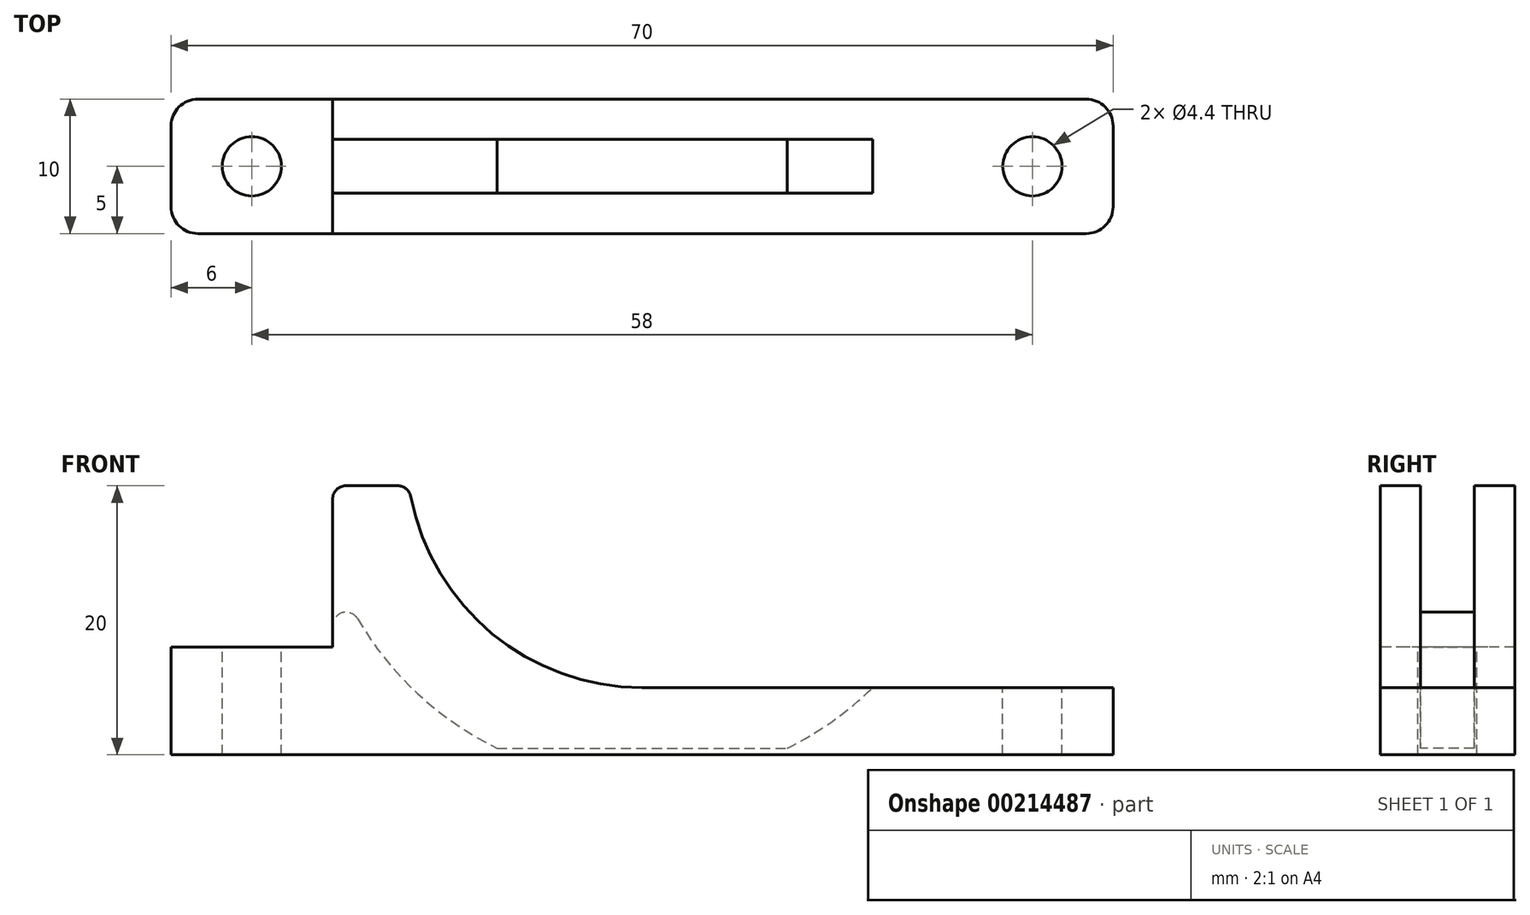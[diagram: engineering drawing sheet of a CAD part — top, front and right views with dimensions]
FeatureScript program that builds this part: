
annotation { "Feature Type Name" : "Feature", "Feature Type Description" : "" }
export const myFeature = defineFeature(function(context is Context, id is Id, definition is map)
    precondition{}
    {
        {
            var Q0;
            Q0=qCreatedBy(makeId("Top.planeOp"),FACE);
            var sketch = newSketch(context, id + "F0", { "sketchPlane" : qUnion([Q0])});
            skLineSegment(sketch, "E0.bottom", {"start": v(35, 5) * mm, "end": v(-35, 5) * mm});
            skLineSegment(sketch, "E0.top", {"start": v(35, -5) * mm, "end": v(-35, -5) * mm});
            skLineSegment(sketch, "E0.left", {"start": v(35, 5) * mm, "end": v(35, -5) * mm});
            skLineSegment(sketch, "E0.right", {"start": v(-35, 5) * mm, "end": v(-35, -5) * mm});
            skPoint(sketch, "E0.middle", {"position": v(0, 0) * mm});
            skSolve(sketch);
        }
        {
            var Q0;
            Q0=makeQuery(id+"F0.imprint","IMPRINT",FACE,{"disambiguationData":[TD([[makeQuery(id+"F0.imprint","IMPRINT",EDGE,{"derivedFrom":sQuery(id+"F0.wireOp",EDGE,"E0.bottom")}),1.0]])]});
            extrude(context, id + "F1", {"entities" : qUnion([Q0]), "depth" : 8 * mm});
        }
        {
            var Q0;
            Q0=makeQuery(id+"F1.opExtrude","CAP_FACE",FACE,{"disambiguationData":[OSD([sQuery(id+"F0.wireOp",EDGE,"E0.bottom"),sQuery(id+"F0.wireOp",EDGE,"E0.top"),sQuery(id+"F0.wireOp",EDGE,"E0.left"),sQuery(id+"F0.wireOp",EDGE,"E0.right")])],"isStart":false});
            var sketch = newSketch(context, id + "F2", { "sketchPlane" : qUnion([Q0])});
            skLineSegment(sketch, "E1.bottom", {"start": v(-23, 5) * mm, "end": v(35, 5) * mm});
            skLineSegment(sketch, "E1.top", {"start": v(-23, -5) * mm, "end": v(35, -5) * mm});
            skLineSegment(sketch, "E1.left", {"start": v(-23, 5) * mm, "end": v(-23, -5) * mm});
            skLineSegment(sketch, "E1.right", {"start": v(35, 5) * mm, "end": v(35, -5) * mm});
            skSolve(sketch);
        }
        {
            var Q0;
            Q0=makeQuery(id+"F2.imprint","IMPRINT",FACE,{"disambiguationData":[TD([[makeQuery(id+"F2.imprint","IMPRINT",EDGE,{"derivedFrom":sQuery(id+"F2.wireOp",EDGE,"E1.bottom")}),1.0]])]});
            extrude(context, id + "F3", {"entities" : qUnion([Q0]), "operationType" : NewBodyOperationType.ADD, "depth" : 12 * mm});
        }
        {
            var Q0;
            Q0=qCreatedBy(makeId("Front.planeOp"),FACE);
            var sketch = newSketch(context, id + "F4", { "sketchPlane" : qUnion([Q0])});
            skCircle(sketch, "E2", {"center": v(0, 22.5) * mm, "radius": 17.5 * mm});
            skCircle(sketch, "E3", {"center": v(0, 22.5) * mm, "radius": 24.5 * mm});
            skLineSegment(sketch, "E4", {"start": v(-10.78, 0.5) * mm, "end": v(10.78, 0.5) * mm});
            skLineSegment(sketch, "E5", {"start": v(36.3, 25) * mm, "end": v(17.32, 25) * mm});
            skLineSegment(sketch, "E6", {"start": v(36.3, 25) * mm, "end": v(36.3, 5) * mm});
            skLineSegment(sketch, "E7", {"start": v(36.3, 5) * mm, "end": v(0, 5) * mm});
            skSolve(sketch);
        }
        {
            var Q0;
            Q0=makeQuery(id+"F4.imprint","IMPRINT",FACE,{"disambiguationData":[TD([[makeQuery(id+"F4.imprint","IMPRINT",EDGE,{"derivedFrom":sQuery(id+"F4.wireOp",EDGE,"E2")}),1.0]])]});
            var Q1;
            {var subQ0=sQuery(id+"F4.wireOp",EDGE,"E5");var subQ1=sQuery(id+"F4.wireOp",EDGE,"E2");var subQ2=makeQuery(id+"F4.imprint","INTERSECT",VERTEX,{"derivedFrom":[subQ1,subQ0]});Q1=makeQuery(id+"F4.imprint","IMPRINT",FACE,{"disambiguationData":[TD([[makeQuery(id+"F4.imprint","IMPRINT",EDGE,{"disambiguationData":[TD([[subQ2,1.0]])],"derivedFrom":subQ1}),-1.0]])]});}
            var Q2;
            {var subQ5=sQuery(id+"F4.wireOp",EDGE,"E6");Q2=makeQuery(id+"F4.imprint","IMPRINT",FACE,{"disambiguationData":[TD([[makeQuery(id+"F4.imprint","IMPRINT",EDGE,{"derivedFrom":subQ5}),-1.0]])]});}
            extrude(context, id + "F5", {"entities" : qUnion([Q0, Q1, Q2]), "operationType" : NewBodyOperationType.REMOVE, "endBound" : BoundingType.SYMMETRIC, "oppositeDirection" : true, "depth" : 15 * mm});
        }
        {
            var Q0;
            {var subQ0=sQuery(id+"F0.wireOp",EDGE,"E0.bottom");var subQ1=sQuery(id+"F0.wireOp",EDGE,"E0.top");var subQ2=sQuery(id+"F0.wireOp",EDGE,"E0.right");Q0=makeQuery(id+"F5.boolean.opBoolean","SPLIT",FACE,{"disambiguationData":[TD([makeQuery(id+"F1.opExtrude","SWEPT_FACE",FACE,{"disambiguationData":[OSD([subQ2])]})])],"derivedFrom":makeQuery(id+"F1.opExtrude","CAP_FACE",FACE,{"disambiguationData":[OSD([subQ0,subQ1,sQuery(id+"F0.wireOp",EDGE,"E0.left"),subQ2])],"isStart":false})});}
            var sketch = newSketch(context, id + "F6", { "sketchPlane" : qUnion([Q0])});
            skPoint(sketch, "E8", {"position": v(-29, 0) * mm});
            skPoint(sketch, "E9.MirrorP", {"position": v(29, 0) * mm});
            skSolve(sketch);
        }
        {
            var Q0;
            Q0=sQuery(id+"F6.wireOp",VERTEX,"E8");
            var Q1;
            Q1=sQuery(id+"F6.wireOp",VERTEX,"E9.MirrorP");
            var Q2;
            Q2=makeQuery(id+"F1.opExtrude","SWEPT_BODY",BODY,{"disambiguationData":[OSD([sQuery(id+"F0.wireOp",EDGE,"E0.bottom"),sQuery(id+"F0.wireOp",EDGE,"E0.top"),sQuery(id+"F0.wireOp",EDGE,"E0.left"),sQuery(id+"F0.wireOp",EDGE,"E0.right")])]});
            hole(context, id + "F7", {"style" : HoleStyle.SIMPLE, "endStyle" : HoleEndStyle.THROUGH, "standardTappedOrClearance" : lookupTablePath({ "standard" : "ISO", "fit" : "Normal", "size" : "M4", "type" : "Clearance" }), "standardBlindInLast" : lookupTablePath({ "fit" : "Standard", "standard" : "ISO", "size" : "M4", "type" : "Clearance" }), "holeDiameter" : 4.4 * mm, "locations" : qUnion([Q0, Q1]), "scope" : qUnion([Q2]), "isTappedThrough" : true});
        }
        {
            var Q0;
            {var subQ0=sQuery(id+"F4.wireOp",EDGE,"E4");Q0=makeQuery(id+"F4.imprint","IMPRINT",FACE,{"disambiguationData":[TD([[makeQuery(id+"F4.imprint","IMPRINT",EDGE,{"derivedFrom":subQ0}),1.0]])]});}
            var Q1;
            {var subQ0=sQuery(id+"F4.wireOp",EDGE,"E5");var subQ1=sQuery(id+"F4.wireOp",EDGE,"E2");var subQ2=makeQuery(id+"F4.imprint","INTERSECT",VERTEX,{"derivedFrom":[subQ1,subQ0]});Q1=makeQuery(id+"F4.imprint","IMPRINT",FACE,{"disambiguationData":[TD([[makeQuery(id+"F4.imprint","IMPRINT",EDGE,{"disambiguationData":[TD([[subQ2,1.0]])],"derivedFrom":subQ1}),-1.0]])]});}
            extrude(context, id + "F8", {"entities" : qUnion([Q0, Q1]), "operationType" : NewBodyOperationType.REMOVE, "endBound" : BoundingType.SYMMETRIC, "oppositeDirection" : true, "depth" : 4 * mm});
        }
        {
            var Q0;
            {var subQ0=sQuery(id+"F4.wireOp",EDGE,"E2");var subQ1=makeQuery(id+"F5.opExtrude","SWEPT_FACE",FACE,{"disambiguationData":[OSD([subQ0])]});var subQ2=sQuery(id+"F2.wireOp",EDGE,"E1.bottom");var subQ3=makeQuery(id+"F3.opExtrude","CAP_FACE",FACE,{"disambiguationData":[OSD([subQ2,sQuery(id+"F2.wireOp",EDGE,"E1.top"),sQuery(id+"F2.wireOp",EDGE,"E1.left"),sQuery(id+"F2.wireOp",EDGE,"E1.right")])],"isStart":false});Q0=makeQuery(id+"F8.boolean.opBoolean","SPLIT",EDGE,{"disambiguationData":[TD([makeQuery(id+"F1.opExtrude","SWEPT_FACE",FACE,{"disambiguationData":[OSD([sQuery(id+"F0.wireOp",EDGE,"E0.bottom")])]})])],"derivedFrom":makeQuery(id+"F5.boolean.opBoolean","INTERSECT",EDGE,{"derivedFrom":[subQ3,subQ1]})});}
            var Q1;
            {var subQ0=sQuery(id+"F4.wireOp",EDGE,"E2");var subQ1=makeQuery(id+"F5.opExtrude","SWEPT_FACE",FACE,{"disambiguationData":[OSD([subQ0])]});var subQ2=sQuery(id+"F2.wireOp",EDGE,"E1.top");var subQ3=makeQuery(id+"F3.opExtrude","CAP_FACE",FACE,{"disambiguationData":[OSD([sQuery(id+"F2.wireOp",EDGE,"E1.bottom"),subQ2,sQuery(id+"F2.wireOp",EDGE,"E1.left"),sQuery(id+"F2.wireOp",EDGE,"E1.right")])],"isStart":false});Q1=makeQuery(id+"F8.boolean.opBoolean","SPLIT",EDGE,{"disambiguationData":[TD([makeQuery(id+"F1.opExtrude","SWEPT_FACE",FACE,{"disambiguationData":[OSD([sQuery(id+"F0.wireOp",EDGE,"E0.top")])]})])],"derivedFrom":makeQuery(id+"F5.boolean.opBoolean","INTERSECT",EDGE,{"derivedFrom":[subQ3,subQ1]})});}
            var Q2;
            {var subQ0=sQuery(id+"F2.wireOp",EDGE,"E1.left");Q2=makeQuery(id+"F8.boolean.opBoolean","SPLIT",EDGE,{"disambiguationData":[TD([makeQuery(id+"F1.opExtrude","SWEPT_FACE",FACE,{"disambiguationData":[OSD([sQuery(id+"F0.wireOp",EDGE,"E0.top")])]})])],"derivedFrom":makeQuery(id+"F3.opExtrude","CAP_EDGE",EDGE,{"disambiguationData":[OSD([subQ0])],"isStart":false})});}
            var Q3;
            {var subQ0=sQuery(id+"F2.wireOp",EDGE,"E1.left");Q3=makeQuery(id+"F8.boolean.opBoolean","SPLIT",EDGE,{"disambiguationData":[TD([makeQuery(id+"F1.opExtrude","SWEPT_FACE",FACE,{"disambiguationData":[OSD([sQuery(id+"F0.wireOp",EDGE,"E0.bottom")])]})])],"derivedFrom":makeQuery(id+"F3.opExtrude","CAP_EDGE",EDGE,{"disambiguationData":[OSD([subQ0])],"isStart":false})});}
            var Q4;
            Q4=makeQuery(id+"F8.boolean.opBoolean","INTERSECT",EDGE,{"derivedFrom":[makeQuery(id+"F3.opExtrude","SWEPT_FACE",FACE,{"disambiguationData":[OSD([sQuery(id+"F2.wireOp",EDGE,"E1.left")])]}),makeQuery(id+"F8.opExtrude","SWEPT_FACE",FACE,{"disambiguationData":[OSD([sQuery(id+"F4.wireOp",EDGE,"E3")])]})]});
            fillet(context, id + "F9", {"entities" : qUnion([Q0, Q1, Q2, Q3, Q4]), "radius" : 1 * mm, "tangentPropagation" : true, "allowEdgeOverflow" : false});
        }
        {
            var Q0;
            Q0=makeQuery(id+"F1.opExtrude","SWEPT_EDGE",EDGE,{"disambiguationData":[OSD([sQuery(id+"F0.wireOp",EDGE,"E0.top"),sQuery(id+"F0.wireOp",EDGE,"E0.right")])]});
            var Q1;
            Q1=makeQuery(id+"F1.opExtrude","SWEPT_EDGE",EDGE,{"disambiguationData":[OSD([sQuery(id+"F0.wireOp",EDGE,"E0.bottom"),sQuery(id+"F0.wireOp",EDGE,"E0.right")])]});
            var Q2;
            Q2=makeQuery(id+"F3.boolean.opBoolean","MERGE",EDGE,{"derivedFrom":[makeQuery(id+"F1.opExtrude","SWEPT_EDGE",EDGE,{"disambiguationData":[OSD([sQuery(id+"F0.wireOp",EDGE,"E0.top"),sQuery(id+"F0.wireOp",EDGE,"E0.left")])]}),makeQuery(id+"F3.opExtrude","SWEPT_EDGE",EDGE,{"disambiguationData":[OSD([sQuery(id+"F2.wireOp",EDGE,"E1.top"),sQuery(id+"F2.wireOp",EDGE,"E1.right")])]})]});
            var Q3;
            Q3=makeQuery(id+"F3.boolean.opBoolean","MERGE",EDGE,{"derivedFrom":[makeQuery(id+"F1.opExtrude","SWEPT_EDGE",EDGE,{"disambiguationData":[OSD([sQuery(id+"F0.wireOp",EDGE,"E0.bottom"),sQuery(id+"F0.wireOp",EDGE,"E0.left")])]}),makeQuery(id+"F3.opExtrude","SWEPT_EDGE",EDGE,{"disambiguationData":[OSD([sQuery(id+"F2.wireOp",EDGE,"E1.bottom"),sQuery(id+"F2.wireOp",EDGE,"E1.right")])]})]});
            fillet(context, id + "F10", {"entities" : qUnion([Q0, Q1, Q2, Q3]), "radius" : 2 * mm, "tangentPropagation" : true, "allowEdgeOverflow" : false});
        }
    });
